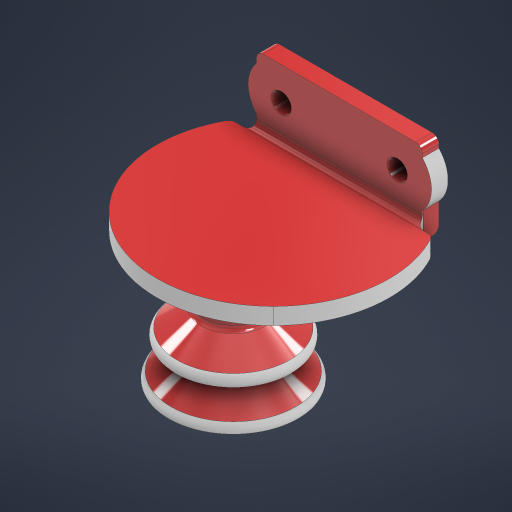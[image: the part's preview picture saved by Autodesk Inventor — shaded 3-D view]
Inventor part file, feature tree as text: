
AUTODESK INVENTOR PART (.ipt)
format: ipt  version: 2024.1 (Build 281209000, 209)  size: 367,616 bytes
history: native  units: in
note: dims shown in document units (in); Inventor stores cm internally (conversion verified against a paired STEP export)
features: extrude x2, fillet x2, sketch x2, projected_geometry x2, imported_body x1, direct_edit x1, other x1
ambient origin geometry x8: Origin, YZ Plane, XZ Plane, XY Plane, X Axis, Y Axis, Z Axis, Center Point
bodies: Solid1 (feature_tree)
feature tree (11):
  imported_body  "Base1"
  direct_edit  "Direct Edit1"
  extrude  "Extrusion1"  Depth=0.3937in TaperAngle=0.0deg
  extrude  "Extrusion2"  Depth=1.9685in
  fillet  "Fillet1"  Radius=1.9685in
  fillet  "Fillet2"  [1 undecoded]
  sketch  "Sketch1"  dims[d0=8.7082in d1=0.3937in d2=0.3937in d3=0.3937in d4=0.0in]
  projected_geometry  "Projected Loop1"
  sketch  "Sketch2"  dims[d5=0.3937in d6=0.0in d7=1.9685in d8=1.9685in]
  projected_geometry  "Projected Loop2"
  other  "Scale1"
note: 1 required parameter value undecoded (feature->parameter linkage not recoverable at this tier; creation-order binding heuristic only, values carry confidence <= 0.55)
